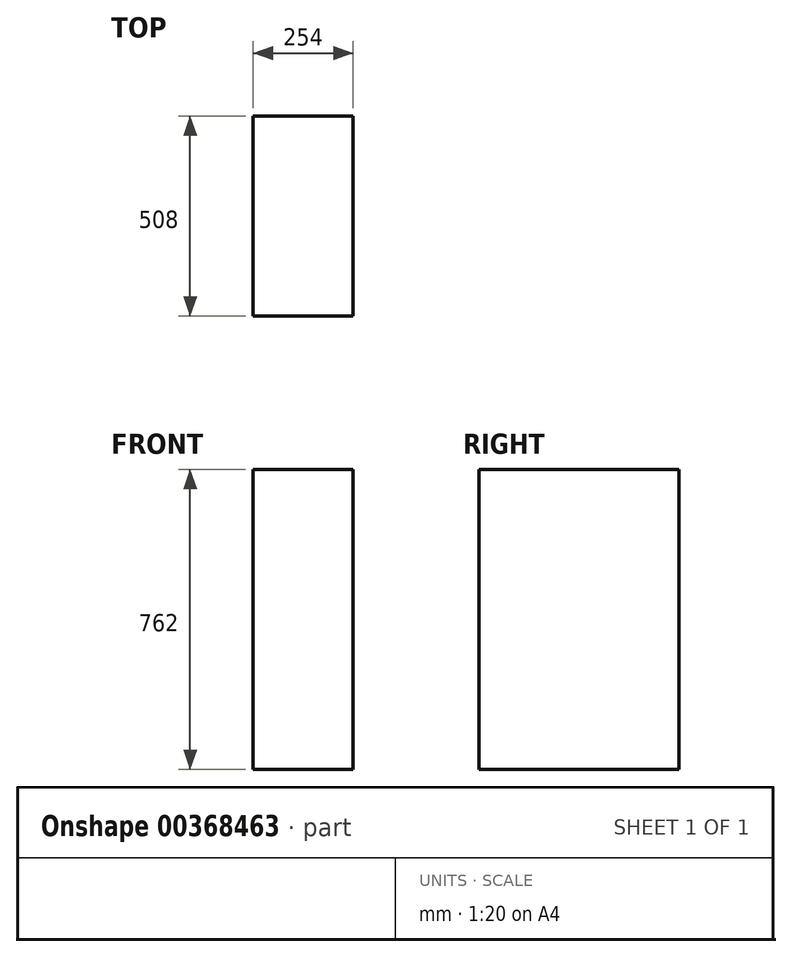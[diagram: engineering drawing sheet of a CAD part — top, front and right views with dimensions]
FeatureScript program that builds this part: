
annotation { "Feature Type Name" : "Feature", "Feature Type Description" : "" }
export const myFeature = defineFeature(function(context is Context, id is Id, definition is map)
    precondition{}
    {
        {
            var Q0;
            Q0=qCreatedBy(makeId("Front.planeOp"),FACE);
            var sketch = newSketch(context, id + "F0", { "sketchPlane" : qUnion([Q0])});
            skLineSegment(sketch, "E0.bottom", {"start": v(127, 381) * mm, "end": v(-127, 381) * mm});
            skLineSegment(sketch, "E0.top", {"start": v(127, -381) * mm, "end": v(-127, -381) * mm});
            skLineSegment(sketch, "E0.left", {"start": v(127, 381) * mm, "end": v(127, -381) * mm});
            skLineSegment(sketch, "E0.right", {"start": v(-127, 381) * mm, "end": v(-127, -381) * mm});
            skPoint(sketch, "E0.middle", {"position": v(0, 0) * mm});
            skSolve(sketch);
        }
        {
            var Q0;
            Q0 = qSketchRegion(id + "F0", true);
            var Q1;
            Q1=makeQuery(id+"F0.imprint","IMPRINT",FACE,{"disambiguationData":[TD([[makeQuery(id+"F0.imprint","IMPRINT",EDGE,{"derivedFrom":sQuery(id+"F0.wireOp",EDGE,"E0.bottom")}),1.0]])]});
            extrude(context, id + "F1", {"entities" : qUnion([Q0, Q1]), "depth" : 508 * mm});
        }
    });
